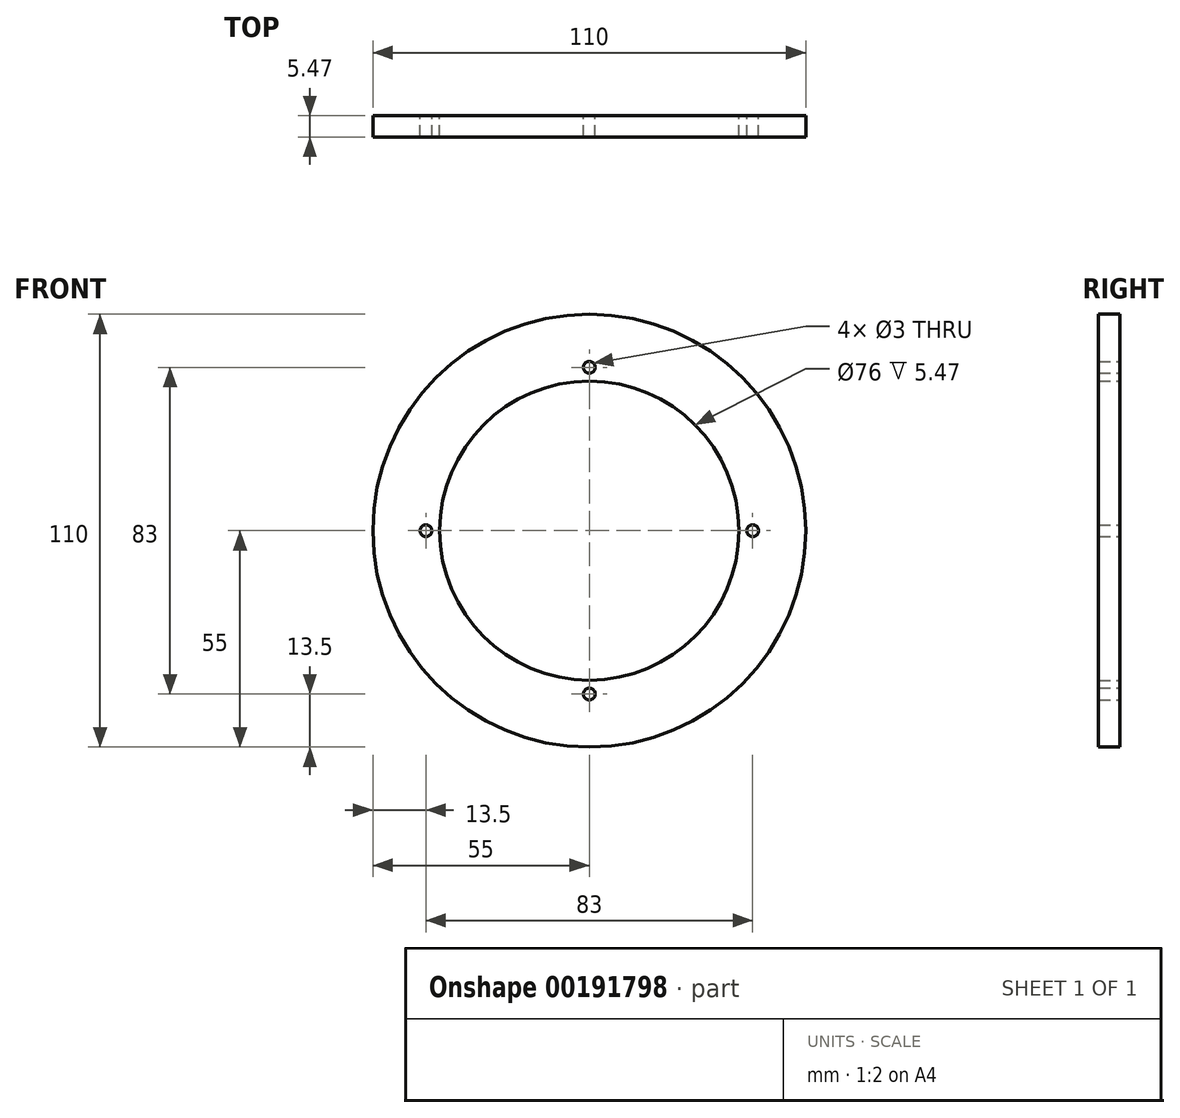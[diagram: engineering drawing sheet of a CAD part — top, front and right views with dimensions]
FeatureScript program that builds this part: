
annotation { "Feature Type Name" : "Feature", "Feature Type Description" : "" }
export const myFeature = defineFeature(function(context is Context, id is Id, definition is map)
    precondition{}
    {
        {
            var Q0;
            Q0=qCreatedBy(makeId("Front.planeOp"),FACE);
            var sketch = newSketch(context, id + "F0", { "sketchPlane" : qUnion([Q0])});
            skCircle(sketch, "E0", {"center": v(0, 0) * mm, "radius": 38 * mm});
            skCircle(sketch, "E1", {"center": v(0, 0) * mm, "radius": 55 * mm});
            skCircle(sketch, "E2", {"center": v(0, 0) * mm, "radius": 41.5 * mm, "construction": true});
            skCircle(sketch, "E3", {"center": v(0, 41.5) * mm, "radius": 1.5 * mm});
            skCircle(sketch, "E4.1.0", {"center": v(-41.5, 0) * mm, "radius": 1.5 * mm});
            skCircle(sketch, "E4.2.0", {"center": v(0, -41.5) * mm, "radius": 1.5 * mm});
            skCircle(sketch, "E4.3.0", {"center": v(41.5, 0) * mm, "radius": 1.5 * mm});
            skSolve(sketch);
        }
        {
            var Q0;
            Q0=makeQuery(id+"F0.imprint","IMPRINT",FACE,{"disambiguationData":[TD([[makeQuery(id+"F0.imprint","IMPRINT",EDGE,{"derivedFrom":sQuery(id+"F0.wireOp",EDGE,"E0")}),-1.0]])]});
            extrude(context, id + "F1", {"entities" : qUnion([Q0]), "depth" : 5.47 * mm});
        }
    });
